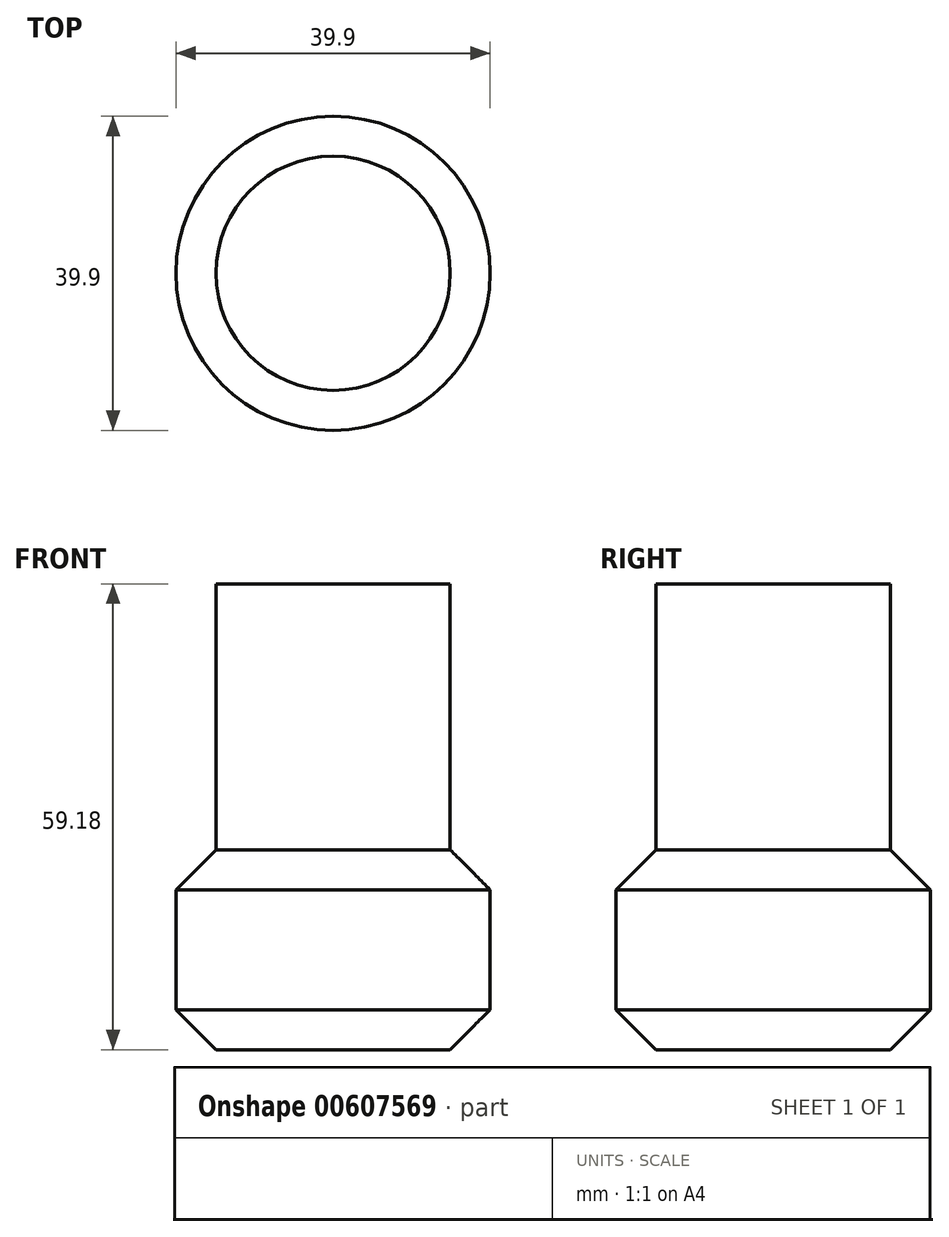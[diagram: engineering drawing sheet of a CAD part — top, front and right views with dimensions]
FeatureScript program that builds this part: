
annotation { "Feature Type Name" : "Feature", "Feature Type Description" : "" }
export const myFeature = defineFeature(function(context is Context, id is Id, definition is map)
    precondition{}
    {
        {
            var Q0;
            Q0=qCreatedBy(makeId("Top.planeOp"),FACE);
            var sketch = newSketch(context, id + "F0", { "sketchPlane" : qUnion([Q0])});
            skCircle(sketch, "E0", {"center": v(0, 0) * mm, "radius": 19.95 * mm});
            skFitSpline(sketch, "E1", {"points": [v(0, 0) * mm, v(-55.36, 94.97) * mm, v(-25.03, 153.28) * mm, v(-124.66, 194.91) * mm], "startDerivative": vector(-255.54, 272.57) * mm, "endDerivative": vector(-408.68, 92.37) * mm});
            skSolve(sketch);
        }
        {
            var Q0;
            Q0=makeQuery(id+"F0.imprint","IMPRINT",FACE,{"disambiguationData":[TD([[makeQuery(id+"F0.imprint","IMPRINT",EDGE,{"derivedFrom":sQuery(id+"F0.wireOp",EDGE,"E0")}),1.0]])]});
            extrude(context, id + "F1", {"entities" : qUnion([Q0]), "depth" : 25.4 * mm, "offsetDistance" : 25.4 * mm});
        }
        {
            var Q0;
            Q0=makeQuery(id+"F1.opExtrude","SWEPT_FACE",FACE,{"disambiguationData":[OSD([sQuery(id+"F0.wireOp",EDGE,"E0")])]});
            chamfer(context, id + "F2", {"entities" : qUnion([Q0]), "width" : 5.08 * mm, "tangentPropagation" : true});
        }
        {
            var Q0;
            Q0=makeQuery(id+"F1.opExtrude","CAP_FACE",FACE,{"disambiguationData":[OSD([sQuery(id+"F0.wireOp",EDGE,"E0")])],"isStart":false});
            extrude(context, id + "F3", {"entities" : qUnion([Q0]), "operationType" : NewBodyOperationType.ADD, "depth" : 33.78 * mm, "offsetDistance" : 25.4 * mm});
        }
    });
